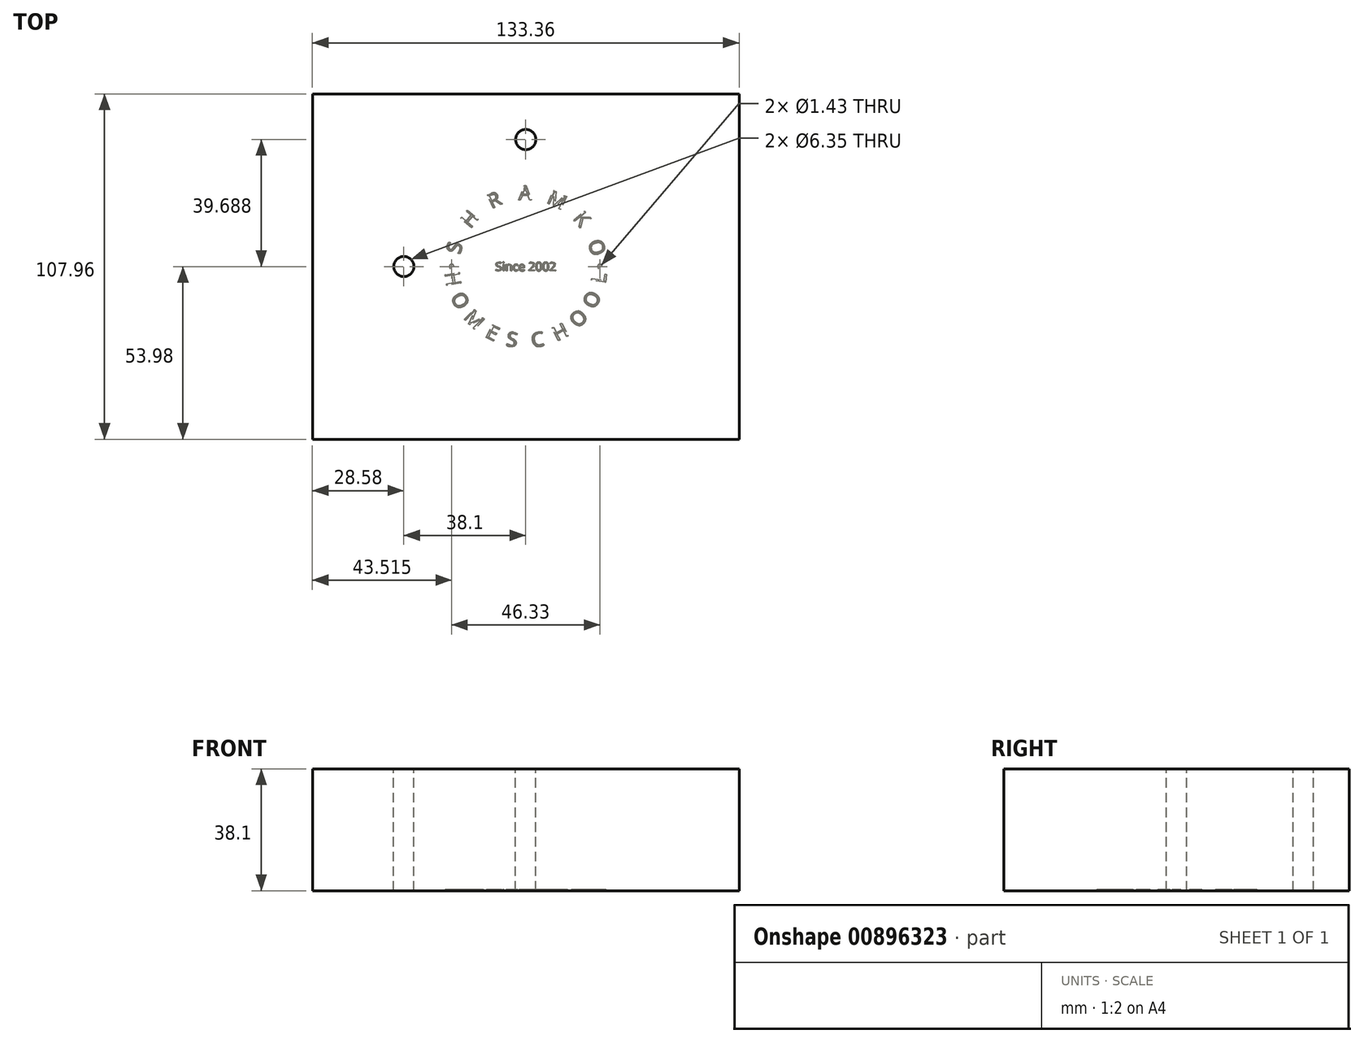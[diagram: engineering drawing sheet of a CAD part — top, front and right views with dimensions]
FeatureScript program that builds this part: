
annotation { "Feature Type Name" : "Feature", "Feature Type Description" : "" }
export const myFeature = defineFeature(function(context is Context, id is Id, definition is map)
    precondition{}
    {
        {
            var Q0;
            Q0=qCreatedBy(makeId("Top.planeOp"),FACE);
            var sketch = newSketch(context, id + "F0", { "sketchPlane" : qUnion([Q0])});
            skLineSegment(sketch, "E0.bottom", {"start": v(66.67, 53.98) * mm, "end": v(-66.68, 53.98) * mm});
            skLineSegment(sketch, "E0.top", {"start": v(66.68, -53.98) * mm, "end": v(-66.67, -53.98) * mm});
            skLineSegment(sketch, "E0.left", {"start": v(66.67, 53.98) * mm, "end": v(66.68, -53.98) * mm});
            skLineSegment(sketch, "E0.right", {"start": v(-66.68, 53.98) * mm, "end": v(-66.67, -53.98) * mm});
            skPoint(sketch, "E0.middle", {"position": v(0, 0) * mm});
            skSolve(sketch);
        }
        {
            var Q0;
            Q0 = qSketchRegion(id + "F0", true);
            extrude(context, id + "F1", {"entities" : qUnion([Q0]), "depth" : 38.1 * mm, "offsetDistance" : 25.4 * mm});
        }
        {
            var Q0;
            Q0=qCreatedBy(makeId("Top.planeOp"),FACE);
            var sketch = newSketch(context, id + "F2", { "sketchPlane" : qUnion([Q0])});
            skCircle(sketch, "E1", {"center": v(0, 0) * mm, "radius": 20.93 * mm, "construction": true});
            skCircle(sketch, "E2", {"center": v(0, 0) * mm, "radius": 25.4 * mm, "construction": true});
            skText(sketch, "E3", { "text": "S", "fontName": "OpenSans-Regular.ttf"});
            skText(sketch, "E4", { "text": "H", "fontName": "OpenSans-Regular.ttf"});
            skText(sketch, "E5", { "text": "R", "fontName": "OpenSans-Regular.ttf"});
            skText(sketch, "E6", { "text": "A", "fontName": "OpenSans-Regular.ttf"});
            skText(sketch, "E7", { "text": "M", "fontName": "OpenSans-Regular.ttf"});
            skText(sketch, "E8", { "text": "K", "fontName": "OpenSans-Regular.ttf"});
            skText(sketch, "E9", { "text": "O", "fontName": "OpenSans-Regular.ttf"});
            skCircle(sketch, "E10", {"center": v(-23.16, 0) * mm, "radius": 0.71 * mm});
            skCircle(sketch, "E11", {"center": v(23.16, 0) * mm, "radius": 0.71 * mm});
            skLineSegment(sketch, "E12", {"start": v(0, 0) * mm, "end": v(0, 25.3) * mm, "construction": true});
            skText(sketch, "E13", { "text": "H", "fontName": "OpenSans-Regular.ttf"});
            skText(sketch, "E14", { "text": "O", "fontName": "OpenSans-Regular.ttf"});
            skText(sketch, "E15", { "text": "M", "fontName": "OpenSans-Regular.ttf"});
            skText(sketch, "E16", { "text": "S", "fontName": "OpenSans-Regular.ttf"});
            skText(sketch, "E17", { "text": "C", "fontName": "OpenSans-Regular.ttf"});
            skText(sketch, "E18", { "text": "O", "fontName": "OpenSans-Regular.ttf"});
            skText(sketch, "E19", { "text": "O", "fontName": "OpenSans-Regular.ttf"});
            skText(sketch, "E20", { "text": "L", "fontName": "OpenSans-Regular.ttf"});
            skText(sketch, "E21", { "text": "E", "fontName": "OpenSans-Regular.ttf"});
            skText(sketch, "E22", { "text": "H", "fontName": "OpenSans-Regular.ttf"});
            const initialGuessF2  = {"E3": [-0.0206, 0.0037, 0.25882, 0.96593, 0.00448], "E4": [-0.01736, 0.0117, 0.64279, 0.76604, 0.0045], "E5": [-0.01068, 0.018, 0.9063, 0.42262, 0.00449], "E6": [-0.0022, 0.02078, 1, 0, 0.00452], "E7": [0.0063, 0.01996, 0.9063, -0.42262, 0.0045], "E8": [0.0146, 0.015, 0.64279, -0.76604, 0.00449], "E9": [0.02505, 0.00418, -0.25882, 0.96593, 0.0045], "E13": [-0.02532, -0.00198, 0.16413, -0.98644, 0.0045], "E14": [-0.02356, -0.00948, 0.46092, -0.88744, 0.0045], "E15": [-0.01966, -0.01609, 0.7126, -0.70157, 0.0045], "E16": [-0.0063, -0.02473, 0.98888, -0.14873, 0.00447], "E17": [0.0021, -0.02531, 0.98644, 0.16413, 0.00449], "E18": [0.0163, -0.01948, 0.70157, 0.7126, 0.0045], "E19": [0.02152, -0.01349, 0.44703, 0.89452, 0.0045], "E20": [0.0248, -0.0055, 0.14873, 0.98888, 0.00448], "E21": [-0.01289, -0.02189, 0.89452, -0.44703, 0.00448], "E22": [0.00971, -0.02347, 0.88744, 0.46092, 0.0045]};
            skSetInitialGuess(sketch, initialGuessF2);
            skSolve(sketch);
        }
        {
            var Q0;
            Q0 = qSketchRegion(id + "F2", true);
            extrude(context, id + "F3", {"entities" : qUnion([Q0]), "operationType" : NewBodyOperationType.REMOVE, "depth" : 0.36 * mm, "offsetDistance" : 25.4 * mm});
        }
        {
            var Q0;
            Q0=makeQuery(id+"F3.boolean.opBoolean","COPY",FACE,{"derivedFrom":makeQuery(id+"F3.opExtrude","CAP_FACE",FACE,{"disambiguationData":[OSD([sQuery(id+"F2.wireOp",EDGE,"E13.sketch_text.stroke-0"),sQuery(id+"F2.wireOp",EDGE,"E13.sketch_text.stroke-1"),sQuery(id+"F2.wireOp",EDGE,"E13.sketch_text.stroke-2"),sQuery(id+"F2.wireOp",EDGE,"E13.sketch_text.stroke-3"),sQuery(id+"F2.wireOp",EDGE,"E13.sketch_text.stroke-4"),sQuery(id+"F2.wireOp",EDGE,"E13.sketch_text.stroke-5"),sQuery(id+"F2.wireOp",EDGE,"E13.sketch_text.stroke-6"),sQuery(id+"F2.wireOp",EDGE,"E13.sketch_text.stroke-7"),sQuery(id+"F2.wireOp",EDGE,"E13.sketch_text.stroke-8"),sQuery(id+"F2.wireOp",EDGE,"E13.sketch_text.stroke-9"),sQuery(id+"F2.wireOp",EDGE,"E13.sketch_text.stroke-10"),sQuery(id+"F2.wireOp",EDGE,"E13.sketch_text.stroke-11")])],"isStart":false})});
            var Q1;
            Q1=makeQuery(id+"F3.boolean.opBoolean","COPY",FACE,{"derivedFrom":makeQuery(id+"F3.opExtrude","CAP_FACE",FACE,{"disambiguationData":[OSD([sQuery(id+"F2.wireOp",EDGE,"E14.sketch_text.stroke-0"),sQuery(id+"F2.wireOp",EDGE,"E14.sketch_text.stroke-1"),sQuery(id+"F2.wireOp",EDGE,"E14.sketch_text.stroke-2"),sQuery(id+"F2.wireOp",EDGE,"E14.sketch_text.stroke-3"),sQuery(id+"F2.wireOp",EDGE,"E14.sketch_text.stroke-4"),sQuery(id+"F2.wireOp",EDGE,"E14.sketch_text.stroke-5"),sQuery(id+"F2.wireOp",EDGE,"E14.sketch_text.stroke-6"),sQuery(id+"F2.wireOp",EDGE,"E14.sketch_text.stroke-7"),sQuery(id+"F2.wireOp",EDGE,"E14.sketch_text.stroke-8"),sQuery(id+"F2.wireOp",EDGE,"E14.sketch_text.stroke-9"),sQuery(id+"F2.wireOp",EDGE,"E14.sketch_text.stroke-10"),sQuery(id+"F2.wireOp",EDGE,"E14.sketch_text.stroke-11"),sQuery(id+"F2.wireOp",EDGE,"E14.sketch_text.stroke-12"),sQuery(id+"F2.wireOp",EDGE,"E14.sketch_text.stroke-13"),sQuery(id+"F2.wireOp",EDGE,"E14.sketch_text.stroke-14"),sQuery(id+"F2.wireOp",EDGE,"E14.sketch_text.stroke-15")])],"isStart":false})});
            var Q2;
            Q2=makeQuery(id+"F3.boolean.opBoolean","COPY",FACE,{"derivedFrom":makeQuery(id+"F3.opExtrude","CAP_FACE",FACE,{"disambiguationData":[OSD([sQuery(id+"F2.wireOp",EDGE,"E15.sketch_text.stroke-0"),sQuery(id+"F2.wireOp",EDGE,"E15.sketch_text.stroke-1"),sQuery(id+"F2.wireOp",EDGE,"E15.sketch_text.stroke-2"),sQuery(id+"F2.wireOp",EDGE,"E15.sketch_text.stroke-3"),sQuery(id+"F2.wireOp",EDGE,"E15.sketch_text.stroke-4"),sQuery(id+"F2.wireOp",EDGE,"E15.sketch_text.stroke-5"),sQuery(id+"F2.wireOp",EDGE,"E15.sketch_text.stroke-6"),sQuery(id+"F2.wireOp",EDGE,"E15.sketch_text.stroke-7"),sQuery(id+"F2.wireOp",EDGE,"E15.sketch_text.stroke-8"),sQuery(id+"F2.wireOp",EDGE,"E15.sketch_text.stroke-9"),sQuery(id+"F2.wireOp",EDGE,"E15.sketch_text.stroke-10"),sQuery(id+"F2.wireOp",EDGE,"E15.sketch_text.stroke-11"),sQuery(id+"F2.wireOp",EDGE,"E15.sketch_text.stroke-12"),sQuery(id+"F2.wireOp",EDGE,"E15.sketch_text.stroke-13"),sQuery(id+"F2.wireOp",EDGE,"E15.sketch_text.stroke-14"),sQuery(id+"F2.wireOp",EDGE,"E15.sketch_text.stroke-15"),sQuery(id+"F2.wireOp",EDGE,"E15.sketch_text.stroke-16"),sQuery(id+"F2.wireOp",EDGE,"E15.sketch_text.stroke-17")])],"isStart":false})});
            var Q3;
            Q3=makeQuery(id+"F3.boolean.opBoolean","COPY",EDGE,{"derivedFrom":makeQuery(id+"F3.opExtrude","CAP_EDGE",EDGE,{"disambiguationData":[OSD([sQuery(id+"F2.wireOp",EDGE,"E10")])],"isStart":false})});
            var Q4;
            Q4=makeQuery(id+"F3.boolean.opBoolean","COPY",FACE,{"derivedFrom":makeQuery(id+"F3.opExtrude","CAP_FACE",FACE,{"disambiguationData":[OSD([sQuery(id+"F2.wireOp",EDGE,"E3.sketch_text.stroke-0"),sQuery(id+"F2.wireOp",EDGE,"E3.sketch_text.stroke-1"),sQuery(id+"F2.wireOp",EDGE,"E3.sketch_text.stroke-2"),sQuery(id+"F2.wireOp",EDGE,"E3.sketch_text.stroke-3"),sQuery(id+"F2.wireOp",EDGE,"E3.sketch_text.stroke-4"),sQuery(id+"F2.wireOp",EDGE,"E3.sketch_text.stroke-5"),sQuery(id+"F2.wireOp",EDGE,"E3.sketch_text.stroke-6"),sQuery(id+"F2.wireOp",EDGE,"E3.sketch_text.stroke-7"),sQuery(id+"F2.wireOp",EDGE,"E3.sketch_text.stroke-8"),sQuery(id+"F2.wireOp",EDGE,"E3.sketch_text.stroke-9"),sQuery(id+"F2.wireOp",EDGE,"E3.sketch_text.stroke-10"),sQuery(id+"F2.wireOp",EDGE,"E3.sketch_text.stroke-11"),sQuery(id+"F2.wireOp",EDGE,"E3.sketch_text.stroke-12"),sQuery(id+"F2.wireOp",EDGE,"E3.sketch_text.stroke-13"),sQuery(id+"F2.wireOp",EDGE,"E3.sketch_text.stroke-14"),sQuery(id+"F2.wireOp",EDGE,"E3.sketch_text.stroke-15"),sQuery(id+"F2.wireOp",EDGE,"E3.sketch_text.stroke-16"),sQuery(id+"F2.wireOp",EDGE,"E3.sketch_text.stroke-17"),sQuery(id+"F2.wireOp",EDGE,"E3.sketch_text.stroke-18"),sQuery(id+"F2.wireOp",EDGE,"E3.sketch_text.stroke-19"),sQuery(id+"F2.wireOp",EDGE,"E3.sketch_text.stroke-20"),sQuery(id+"F2.wireOp",EDGE,"E3.sketch_text.stroke-21"),sQuery(id+"F2.wireOp",EDGE,"E3.sketch_text.stroke-22"),sQuery(id+"F2.wireOp",EDGE,"E3.sketch_text.stroke-23"),sQuery(id+"F2.wireOp",EDGE,"E3.sketch_text.stroke-24")])],"isStart":false})});
            var Q5;
            Q5=makeQuery(id+"F3.boolean.opBoolean","COPY",FACE,{"derivedFrom":makeQuery(id+"F3.opExtrude","CAP_FACE",FACE,{"disambiguationData":[OSD([sQuery(id+"F2.wireOp",EDGE,"E4.sketch_text.stroke-0"),sQuery(id+"F2.wireOp",EDGE,"E4.sketch_text.stroke-1"),sQuery(id+"F2.wireOp",EDGE,"E4.sketch_text.stroke-2"),sQuery(id+"F2.wireOp",EDGE,"E4.sketch_text.stroke-3"),sQuery(id+"F2.wireOp",EDGE,"E4.sketch_text.stroke-4"),sQuery(id+"F2.wireOp",EDGE,"E4.sketch_text.stroke-5"),sQuery(id+"F2.wireOp",EDGE,"E4.sketch_text.stroke-6"),sQuery(id+"F2.wireOp",EDGE,"E4.sketch_text.stroke-7"),sQuery(id+"F2.wireOp",EDGE,"E4.sketch_text.stroke-8"),sQuery(id+"F2.wireOp",EDGE,"E4.sketch_text.stroke-9"),sQuery(id+"F2.wireOp",EDGE,"E4.sketch_text.stroke-10"),sQuery(id+"F2.wireOp",EDGE,"E4.sketch_text.stroke-11")])],"isStart":false})});
            var Q6;
            Q6=makeQuery(id+"F3.boolean.opBoolean","COPY",FACE,{"derivedFrom":makeQuery(id+"F3.opExtrude","CAP_FACE",FACE,{"disambiguationData":[OSD([sQuery(id+"F2.wireOp",EDGE,"E5.sketch_text.stroke-0"),sQuery(id+"F2.wireOp",EDGE,"E5.sketch_text.stroke-1"),sQuery(id+"F2.wireOp",EDGE,"E5.sketch_text.stroke-2"),sQuery(id+"F2.wireOp",EDGE,"E5.sketch_text.stroke-3"),sQuery(id+"F2.wireOp",EDGE,"E5.sketch_text.stroke-4"),sQuery(id+"F2.wireOp",EDGE,"E5.sketch_text.stroke-5"),sQuery(id+"F2.wireOp",EDGE,"E5.sketch_text.stroke-6"),sQuery(id+"F2.wireOp",EDGE,"E5.sketch_text.stroke-7"),sQuery(id+"F2.wireOp",EDGE,"E5.sketch_text.stroke-8"),sQuery(id+"F2.wireOp",EDGE,"E5.sketch_text.stroke-9"),sQuery(id+"F2.wireOp",EDGE,"E5.sketch_text.stroke-10"),sQuery(id+"F2.wireOp",EDGE,"E5.sketch_text.stroke-11"),sQuery(id+"F2.wireOp",EDGE,"E5.sketch_text.stroke-12"),sQuery(id+"F2.wireOp",EDGE,"E5.sketch_text.stroke-13"),sQuery(id+"F2.wireOp",EDGE,"E5.sketch_text.stroke-14"),sQuery(id+"F2.wireOp",EDGE,"E5.sketch_text.stroke-15"),sQuery(id+"F2.wireOp",EDGE,"E5.sketch_text.stroke-16"),sQuery(id+"F2.wireOp",EDGE,"E5.sketch_text.stroke-17")])],"isStart":false})});
            var Q7;
            Q7=makeQuery(id+"F3.boolean.opBoolean","COPY",FACE,{"derivedFrom":makeQuery(id+"F3.opExtrude","CAP_FACE",FACE,{"disambiguationData":[OSD([sQuery(id+"F2.wireOp",EDGE,"E6.sketch_text.stroke-0"),sQuery(id+"F2.wireOp",EDGE,"E6.sketch_text.stroke-1"),sQuery(id+"F2.wireOp",EDGE,"E6.sketch_text.stroke-2"),sQuery(id+"F2.wireOp",EDGE,"E6.sketch_text.stroke-3"),sQuery(id+"F2.wireOp",EDGE,"E6.sketch_text.stroke-4"),sQuery(id+"F2.wireOp",EDGE,"E6.sketch_text.stroke-5"),sQuery(id+"F2.wireOp",EDGE,"E6.sketch_text.stroke-6"),sQuery(id+"F2.wireOp",EDGE,"E6.sketch_text.stroke-7"),sQuery(id+"F2.wireOp",EDGE,"E6.sketch_text.stroke-8"),sQuery(id+"F2.wireOp",EDGE,"E6.sketch_text.stroke-9"),sQuery(id+"F2.wireOp",EDGE,"E6.sketch_text.stroke-10"),sQuery(id+"F2.wireOp",EDGE,"E6.sketch_text.stroke-11"),sQuery(id+"F2.wireOp",EDGE,"E6.sketch_text.stroke-12")])],"isStart":false})});
            var Q8;
            Q8=makeQuery(id+"F3.boolean.opBoolean","COPY",FACE,{"derivedFrom":makeQuery(id+"F3.opExtrude","CAP_FACE",FACE,{"disambiguationData":[OSD([sQuery(id+"F2.wireOp",EDGE,"E7.sketch_text.stroke-0"),sQuery(id+"F2.wireOp",EDGE,"E7.sketch_text.stroke-1"),sQuery(id+"F2.wireOp",EDGE,"E7.sketch_text.stroke-2"),sQuery(id+"F2.wireOp",EDGE,"E7.sketch_text.stroke-3"),sQuery(id+"F2.wireOp",EDGE,"E7.sketch_text.stroke-4"),sQuery(id+"F2.wireOp",EDGE,"E7.sketch_text.stroke-5"),sQuery(id+"F2.wireOp",EDGE,"E7.sketch_text.stroke-6"),sQuery(id+"F2.wireOp",EDGE,"E7.sketch_text.stroke-7"),sQuery(id+"F2.wireOp",EDGE,"E7.sketch_text.stroke-8"),sQuery(id+"F2.wireOp",EDGE,"E7.sketch_text.stroke-9"),sQuery(id+"F2.wireOp",EDGE,"E7.sketch_text.stroke-10"),sQuery(id+"F2.wireOp",EDGE,"E7.sketch_text.stroke-11"),sQuery(id+"F2.wireOp",EDGE,"E7.sketch_text.stroke-12"),sQuery(id+"F2.wireOp",EDGE,"E7.sketch_text.stroke-13"),sQuery(id+"F2.wireOp",EDGE,"E7.sketch_text.stroke-14"),sQuery(id+"F2.wireOp",EDGE,"E7.sketch_text.stroke-15"),sQuery(id+"F2.wireOp",EDGE,"E7.sketch_text.stroke-16"),sQuery(id+"F2.wireOp",EDGE,"E7.sketch_text.stroke-17")])],"isStart":false})});
            var Q9;
            Q9=makeQuery(id+"F3.boolean.opBoolean","COPY",FACE,{"derivedFrom":makeQuery(id+"F3.opExtrude","CAP_FACE",FACE,{"disambiguationData":[OSD([sQuery(id+"F2.wireOp",EDGE,"E8.sketch_text.stroke-0"),sQuery(id+"F2.wireOp",EDGE,"E8.sketch_text.stroke-1"),sQuery(id+"F2.wireOp",EDGE,"E8.sketch_text.stroke-2"),sQuery(id+"F2.wireOp",EDGE,"E8.sketch_text.stroke-3"),sQuery(id+"F2.wireOp",EDGE,"E8.sketch_text.stroke-4"),sQuery(id+"F2.wireOp",EDGE,"E8.sketch_text.stroke-5"),sQuery(id+"F2.wireOp",EDGE,"E8.sketch_text.stroke-6"),sQuery(id+"F2.wireOp",EDGE,"E8.sketch_text.stroke-7"),sQuery(id+"F2.wireOp",EDGE,"E8.sketch_text.stroke-8"),sQuery(id+"F2.wireOp",EDGE,"E8.sketch_text.stroke-9"),sQuery(id+"F2.wireOp",EDGE,"E8.sketch_text.stroke-10"),sQuery(id+"F2.wireOp",EDGE,"E8.sketch_text.stroke-11")])],"isStart":false})});
            var Q10;
            Q10=makeQuery(id+"F3.boolean.opBoolean","COPY",FACE,{"derivedFrom":makeQuery(id+"F3.opExtrude","CAP_FACE",FACE,{"disambiguationData":[OSD([sQuery(id+"F2.wireOp",EDGE,"E21.sketch_text.stroke-0"),sQuery(id+"F2.wireOp",EDGE,"E21.sketch_text.stroke-1"),sQuery(id+"F2.wireOp",EDGE,"E21.sketch_text.stroke-2"),sQuery(id+"F2.wireOp",EDGE,"E21.sketch_text.stroke-3"),sQuery(id+"F2.wireOp",EDGE,"E21.sketch_text.stroke-4"),sQuery(id+"F2.wireOp",EDGE,"E21.sketch_text.stroke-5"),sQuery(id+"F2.wireOp",EDGE,"E21.sketch_text.stroke-6"),sQuery(id+"F2.wireOp",EDGE,"E21.sketch_text.stroke-7"),sQuery(id+"F2.wireOp",EDGE,"E21.sketch_text.stroke-8"),sQuery(id+"F2.wireOp",EDGE,"E21.sketch_text.stroke-9"),sQuery(id+"F2.wireOp",EDGE,"E21.sketch_text.stroke-10"),sQuery(id+"F2.wireOp",EDGE,"E21.sketch_text.stroke-11")])],"isStart":false})});
            var Q11;
            Q11=makeQuery(id+"F3.boolean.opBoolean","COPY",FACE,{"derivedFrom":makeQuery(id+"F3.opExtrude","CAP_FACE",FACE,{"disambiguationData":[OSD([sQuery(id+"F2.wireOp",EDGE,"E18.sketch_text.stroke-0"),sQuery(id+"F2.wireOp",EDGE,"E18.sketch_text.stroke-1"),sQuery(id+"F2.wireOp",EDGE,"E18.sketch_text.stroke-2"),sQuery(id+"F2.wireOp",EDGE,"E18.sketch_text.stroke-3"),sQuery(id+"F2.wireOp",EDGE,"E18.sketch_text.stroke-4"),sQuery(id+"F2.wireOp",EDGE,"E18.sketch_text.stroke-5"),sQuery(id+"F2.wireOp",EDGE,"E18.sketch_text.stroke-6"),sQuery(id+"F2.wireOp",EDGE,"E18.sketch_text.stroke-7"),sQuery(id+"F2.wireOp",EDGE,"E18.sketch_text.stroke-8"),sQuery(id+"F2.wireOp",EDGE,"E18.sketch_text.stroke-9"),sQuery(id+"F2.wireOp",EDGE,"E18.sketch_text.stroke-10"),sQuery(id+"F2.wireOp",EDGE,"E18.sketch_text.stroke-11"),sQuery(id+"F2.wireOp",EDGE,"E18.sketch_text.stroke-12"),sQuery(id+"F2.wireOp",EDGE,"E18.sketch_text.stroke-13"),sQuery(id+"F2.wireOp",EDGE,"E18.sketch_text.stroke-14"),sQuery(id+"F2.wireOp",EDGE,"E18.sketch_text.stroke-15")])],"isStart":false})});
            var Q12;
            Q12=makeQuery(id+"F3.boolean.opBoolean","COPY",FACE,{"derivedFrom":makeQuery(id+"F3.opExtrude","CAP_FACE",FACE,{"disambiguationData":[OSD([sQuery(id+"F2.wireOp",EDGE,"E17.sketch_text.stroke-0"),sQuery(id+"F2.wireOp",EDGE,"E17.sketch_text.stroke-1"),sQuery(id+"F2.wireOp",EDGE,"E17.sketch_text.stroke-2"),sQuery(id+"F2.wireOp",EDGE,"E17.sketch_text.stroke-3"),sQuery(id+"F2.wireOp",EDGE,"E17.sketch_text.stroke-4"),sQuery(id+"F2.wireOp",EDGE,"E17.sketch_text.stroke-5"),sQuery(id+"F2.wireOp",EDGE,"E17.sketch_text.stroke-6"),sQuery(id+"F2.wireOp",EDGE,"E17.sketch_text.stroke-7"),sQuery(id+"F2.wireOp",EDGE,"E17.sketch_text.stroke-8"),sQuery(id+"F2.wireOp",EDGE,"E17.sketch_text.stroke-9"),sQuery(id+"F2.wireOp",EDGE,"E17.sketch_text.stroke-10"),sQuery(id+"F2.wireOp",EDGE,"E17.sketch_text.stroke-11"),sQuery(id+"F2.wireOp",EDGE,"E17.sketch_text.stroke-12"),sQuery(id+"F2.wireOp",EDGE,"E17.sketch_text.stroke-13"),sQuery(id+"F2.wireOp",EDGE,"E17.sketch_text.stroke-14")])],"isStart":false})});
            var Q13;
            Q13=makeQuery(id+"F3.boolean.opBoolean","COPY",FACE,{"derivedFrom":makeQuery(id+"F3.opExtrude","CAP_FACE",FACE,{"disambiguationData":[OSD([sQuery(id+"F2.wireOp",EDGE,"E16.sketch_text.stroke-0"),sQuery(id+"F2.wireOp",EDGE,"E16.sketch_text.stroke-1"),sQuery(id+"F2.wireOp",EDGE,"E16.sketch_text.stroke-2"),sQuery(id+"F2.wireOp",EDGE,"E16.sketch_text.stroke-3"),sQuery(id+"F2.wireOp",EDGE,"E16.sketch_text.stroke-4"),sQuery(id+"F2.wireOp",EDGE,"E16.sketch_text.stroke-5"),sQuery(id+"F2.wireOp",EDGE,"E16.sketch_text.stroke-6"),sQuery(id+"F2.wireOp",EDGE,"E16.sketch_text.stroke-7"),sQuery(id+"F2.wireOp",EDGE,"E16.sketch_text.stroke-8"),sQuery(id+"F2.wireOp",EDGE,"E16.sketch_text.stroke-9"),sQuery(id+"F2.wireOp",EDGE,"E16.sketch_text.stroke-10"),sQuery(id+"F2.wireOp",EDGE,"E16.sketch_text.stroke-11"),sQuery(id+"F2.wireOp",EDGE,"E16.sketch_text.stroke-12"),sQuery(id+"F2.wireOp",EDGE,"E16.sketch_text.stroke-13"),sQuery(id+"F2.wireOp",EDGE,"E16.sketch_text.stroke-14"),sQuery(id+"F2.wireOp",EDGE,"E16.sketch_text.stroke-15"),sQuery(id+"F2.wireOp",EDGE,"E16.sketch_text.stroke-16"),sQuery(id+"F2.wireOp",EDGE,"E16.sketch_text.stroke-17"),sQuery(id+"F2.wireOp",EDGE,"E16.sketch_text.stroke-18"),sQuery(id+"F2.wireOp",EDGE,"E16.sketch_text.stroke-19"),sQuery(id+"F2.wireOp",EDGE,"E16.sketch_text.stroke-20"),sQuery(id+"F2.wireOp",EDGE,"E16.sketch_text.stroke-21"),sQuery(id+"F2.wireOp",EDGE,"E16.sketch_text.stroke-22"),sQuery(id+"F2.wireOp",EDGE,"E16.sketch_text.stroke-23"),sQuery(id+"F2.wireOp",EDGE,"E16.sketch_text.stroke-24")])],"isStart":false})});
            var Q14;
            Q14=makeQuery(id+"F3.boolean.opBoolean","COPY",FACE,{"derivedFrom":makeQuery(id+"F3.opExtrude","CAP_FACE",FACE,{"disambiguationData":[OSD([sQuery(id+"F2.wireOp",EDGE,"E19.sketch_text.stroke-0"),sQuery(id+"F2.wireOp",EDGE,"E19.sketch_text.stroke-1"),sQuery(id+"F2.wireOp",EDGE,"E19.sketch_text.stroke-2"),sQuery(id+"F2.wireOp",EDGE,"E19.sketch_text.stroke-3"),sQuery(id+"F2.wireOp",EDGE,"E19.sketch_text.stroke-4"),sQuery(id+"F2.wireOp",EDGE,"E19.sketch_text.stroke-5"),sQuery(id+"F2.wireOp",EDGE,"E19.sketch_text.stroke-6"),sQuery(id+"F2.wireOp",EDGE,"E19.sketch_text.stroke-7"),sQuery(id+"F2.wireOp",EDGE,"E19.sketch_text.stroke-8"),sQuery(id+"F2.wireOp",EDGE,"E19.sketch_text.stroke-9"),sQuery(id+"F2.wireOp",EDGE,"E19.sketch_text.stroke-10"),sQuery(id+"F2.wireOp",EDGE,"E19.sketch_text.stroke-11"),sQuery(id+"F2.wireOp",EDGE,"E19.sketch_text.stroke-12"),sQuery(id+"F2.wireOp",EDGE,"E19.sketch_text.stroke-13"),sQuery(id+"F2.wireOp",EDGE,"E19.sketch_text.stroke-14"),sQuery(id+"F2.wireOp",EDGE,"E19.sketch_text.stroke-15")])],"isStart":false})});
            var Q15;
            Q15=makeQuery(id+"F3.boolean.opBoolean","COPY",FACE,{"derivedFrom":makeQuery(id+"F3.opExtrude","CAP_FACE",FACE,{"disambiguationData":[OSD([sQuery(id+"F2.wireOp",EDGE,"E20.sketch_text.stroke-0"),sQuery(id+"F2.wireOp",EDGE,"E20.sketch_text.stroke-1"),sQuery(id+"F2.wireOp",EDGE,"E20.sketch_text.stroke-2"),sQuery(id+"F2.wireOp",EDGE,"E20.sketch_text.stroke-3"),sQuery(id+"F2.wireOp",EDGE,"E20.sketch_text.stroke-4"),sQuery(id+"F2.wireOp",EDGE,"E20.sketch_text.stroke-5")])],"isStart":false})});
            var Q16;
            Q16=makeQuery(id+"F3.boolean.opBoolean","COPY",FACE,{"derivedFrom":makeQuery(id+"F3.opExtrude","CAP_FACE",FACE,{"disambiguationData":[OSD([sQuery(id+"F2.wireOp",EDGE,"E9.sketch_text.stroke-0"),sQuery(id+"F2.wireOp",EDGE,"E9.sketch_text.stroke-1"),sQuery(id+"F2.wireOp",EDGE,"E9.sketch_text.stroke-2"),sQuery(id+"F2.wireOp",EDGE,"E9.sketch_text.stroke-3"),sQuery(id+"F2.wireOp",EDGE,"E9.sketch_text.stroke-4"),sQuery(id+"F2.wireOp",EDGE,"E9.sketch_text.stroke-5"),sQuery(id+"F2.wireOp",EDGE,"E9.sketch_text.stroke-6"),sQuery(id+"F2.wireOp",EDGE,"E9.sketch_text.stroke-7"),sQuery(id+"F2.wireOp",EDGE,"E9.sketch_text.stroke-8"),sQuery(id+"F2.wireOp",EDGE,"E9.sketch_text.stroke-9"),sQuery(id+"F2.wireOp",EDGE,"E9.sketch_text.stroke-10"),sQuery(id+"F2.wireOp",EDGE,"E9.sketch_text.stroke-11"),sQuery(id+"F2.wireOp",EDGE,"E9.sketch_text.stroke-12"),sQuery(id+"F2.wireOp",EDGE,"E9.sketch_text.stroke-13"),sQuery(id+"F2.wireOp",EDGE,"E9.sketch_text.stroke-14"),sQuery(id+"F2.wireOp",EDGE,"E9.sketch_text.stroke-15")])],"isStart":false})});
            var Q17;
            Q17=makeQuery(id+"F3.boolean.opBoolean","COPY",FACE,{"derivedFrom":makeQuery(id+"F3.opExtrude","CAP_FACE",FACE,{"disambiguationData":[OSD([sQuery(id+"F2.wireOp",EDGE,"E22.sketch_text.stroke-0"),sQuery(id+"F2.wireOp",EDGE,"E22.sketch_text.stroke-1"),sQuery(id+"F2.wireOp",EDGE,"E22.sketch_text.stroke-2"),sQuery(id+"F2.wireOp",EDGE,"E22.sketch_text.stroke-3"),sQuery(id+"F2.wireOp",EDGE,"E22.sketch_text.stroke-4"),sQuery(id+"F2.wireOp",EDGE,"E22.sketch_text.stroke-5"),sQuery(id+"F2.wireOp",EDGE,"E22.sketch_text.stroke-6"),sQuery(id+"F2.wireOp",EDGE,"E22.sketch_text.stroke-7"),sQuery(id+"F2.wireOp",EDGE,"E22.sketch_text.stroke-8"),sQuery(id+"F2.wireOp",EDGE,"E22.sketch_text.stroke-9"),sQuery(id+"F2.wireOp",EDGE,"E22.sketch_text.stroke-10"),sQuery(id+"F2.wireOp",EDGE,"E22.sketch_text.stroke-11")])],"isStart":false})});
            var Q18;
            Q18=makeQuery(id+"F3.boolean.opBoolean","COPY",EDGE,{"derivedFrom":makeQuery(id+"F3.opExtrude","CAP_EDGE",EDGE,{"disambiguationData":[OSD([sQuery(id+"F2.wireOp",EDGE,"E11")])],"isStart":false})});
            fillet(context, id + "F4", {"entities" : qUnion([Q0, Q1, Q2, Q3, Q4, Q5, Q6, Q7, Q8, Q9, Q10, Q11, Q12, Q13, Q14, Q15, Q16, Q17, Q18]), "radius" : 0.2 * mm, "tangentPropagation" : true, "allowEdgeOverflow" : false});
        }
        {
            var Q0;
            Q0=makeQuery(id+"F1.opExtrude","CAP_FACE",FACE,{"disambiguationData":[OSD([sQuery(id+"F0.wireOp",EDGE,"E0.bottom"),sQuery(id+"F0.wireOp",EDGE,"E0.top"),sQuery(id+"F0.wireOp",EDGE,"E0.left"),sQuery(id+"F0.wireOp",EDGE,"E0.right")])],"isStart":false});
            var sketch = newSketch(context, id + "F5", { "sketchPlane" : qUnion([Q0])});
            skCircle(sketch, "E23", {"center": v(-38.1, 0) * mm, "radius": 3.18 * mm});
            skCircle(sketch, "E24", {"center": v(0, 39.69) * mm, "radius": 3.18 * mm});
            skLineSegment(sketch, "E25", {"start": v(-38.1, 0) * mm, "end": v(0, 0) * mm, "construction": true});
            skLineSegment(sketch, "E26", {"start": v(0, 0) * mm, "end": v(0, 39.69) * mm, "construction": true});
            skLineSegment(sketch, "E27.bottom", {"start": v(66.68, 53.97) * mm, "end": v(-66.68, 53.97) * mm, "construction": true});
            skLineSegment(sketch, "E27.top", {"start": v(66.68, -53.98) * mm, "end": v(-66.68, -53.98) * mm, "construction": true});
            skLineSegment(sketch, "E27.left", {"start": v(66.67, 53.97) * mm, "end": v(66.68, -53.97) * mm, "construction": true});
            skLineSegment(sketch, "E27.right", {"start": v(-66.68, 53.97) * mm, "end": v(-66.68, -53.97) * mm, "construction": true});
            skPoint(sketch, "E27.middle", {"position": v(0, 0) * mm});
            skSolve(sketch);
        }
        {
            var Q0;
            Q0 = qSketchRegion(id + "F5", true);
            extrude(context, id + "F6", {"entities" : qUnion([Q0]), "operationType" : NewBodyOperationType.REMOVE, "endBound" : BoundingType.THROUGH_ALL, "oppositeDirection" : true, "depth" : 25.4 * mm, "offsetDistance" : 25.4 * mm});
        }
        {
            var Q0;
            Q0=qCreatedBy(makeId("Top.planeOp"),FACE);
            var sketch = newSketch(context, id + "F7", { "sketchPlane" : qUnion([Q0])});
            skText(sketch, "E28", { "text": "Since 2002", "fontName": "OpenSans-Regular.ttf"});
            const initialGuessF7  = {"E28": [-0.00952, -0.00137, 1, 0, 0.00274]};
            skSetInitialGuess(sketch, initialGuessF7);
            skSolve(sketch);
        }
        {
            var Q0;
            Q0 = qSketchRegion(id + "F7", true);
            extrude(context, id + "F8", {"entities" : qUnion([Q0]), "operationType" : NewBodyOperationType.REMOVE, "depth" : 0.36 * mm, "offsetDistance" : 25.4 * mm});
        }
        {
            var Q0;
            Q0=makeQuery(id+"F8.boolean.opBoolean","COPY",FACE,{"derivedFrom":makeQuery(id+"F8.opExtrude","CAP_FACE",FACE,{"disambiguationData":[OSD([sQuery(id+"F7.wireOp",EDGE,"E28.sketch_text.stroke-0"),sQuery(id+"F7.wireOp",EDGE,"E28.sketch_text.stroke-1"),sQuery(id+"F7.wireOp",EDGE,"E28.sketch_text.stroke-2"),sQuery(id+"F7.wireOp",EDGE,"E28.sketch_text.stroke-3"),sQuery(id+"F7.wireOp",EDGE,"E28.sketch_text.stroke-4"),sQuery(id+"F7.wireOp",EDGE,"E28.sketch_text.stroke-5"),sQuery(id+"F7.wireOp",EDGE,"E28.sketch_text.stroke-6"),sQuery(id+"F7.wireOp",EDGE,"E28.sketch_text.stroke-7"),sQuery(id+"F7.wireOp",EDGE,"E28.sketch_text.stroke-8"),sQuery(id+"F7.wireOp",EDGE,"E28.sketch_text.stroke-9"),sQuery(id+"F7.wireOp",EDGE,"E28.sketch_text.stroke-10"),sQuery(id+"F7.wireOp",EDGE,"E28.sketch_text.stroke-11"),sQuery(id+"F7.wireOp",EDGE,"E28.sketch_text.stroke-12"),sQuery(id+"F7.wireOp",EDGE,"E28.sketch_text.stroke-13"),sQuery(id+"F7.wireOp",EDGE,"E28.sketch_text.stroke-14"),sQuery(id+"F7.wireOp",EDGE,"E28.sketch_text.stroke-15"),sQuery(id+"F7.wireOp",EDGE,"E28.sketch_text.stroke-16"),sQuery(id+"F7.wireOp",EDGE,"E28.sketch_text.stroke-17"),sQuery(id+"F7.wireOp",EDGE,"E28.sketch_text.stroke-18"),sQuery(id+"F7.wireOp",EDGE,"E28.sketch_text.stroke-19"),sQuery(id+"F7.wireOp",EDGE,"E28.sketch_text.stroke-20"),sQuery(id+"F7.wireOp",EDGE,"E28.sketch_text.stroke-21"),sQuery(id+"F7.wireOp",EDGE,"E28.sketch_text.stroke-22"),sQuery(id+"F7.wireOp",EDGE,"E28.sketch_text.stroke-23"),sQuery(id+"F7.wireOp",EDGE,"E28.sketch_text.stroke-24")])],"isStart":false})});
            var Q1;
            Q1=makeQuery(id+"F8.boolean.opBoolean","COPY",FACE,{"derivedFrom":makeQuery(id+"F8.opExtrude","CAP_FACE",FACE,{"disambiguationData":[OSD([sQuery(id+"F7.wireOp",EDGE,"E28.sketch_text.stroke-25"),sQuery(id+"F7.wireOp",EDGE,"E28.sketch_text.stroke-26"),sQuery(id+"F7.wireOp",EDGE,"E28.sketch_text.stroke-27"),sQuery(id+"F7.wireOp",EDGE,"E28.sketch_text.stroke-28")])],"isStart":false})});
            var Q2;
            Q2=makeQuery(id+"F8.boolean.opBoolean","COPY",FACE,{"derivedFrom":makeQuery(id+"F8.opExtrude","CAP_FACE",FACE,{"disambiguationData":[OSD([sQuery(id+"F7.wireOp",EDGE,"E28.sketch_text.stroke-37"),sQuery(id+"F7.wireOp",EDGE,"E28.sketch_text.stroke-38"),sQuery(id+"F7.wireOp",EDGE,"E28.sketch_text.stroke-39"),sQuery(id+"F7.wireOp",EDGE,"E28.sketch_text.stroke-40"),sQuery(id+"F7.wireOp",EDGE,"E28.sketch_text.stroke-41"),sQuery(id+"F7.wireOp",EDGE,"E28.sketch_text.stroke-42"),sQuery(id+"F7.wireOp",EDGE,"E28.sketch_text.stroke-43"),sQuery(id+"F7.wireOp",EDGE,"E28.sketch_text.stroke-44"),sQuery(id+"F7.wireOp",EDGE,"E28.sketch_text.stroke-45"),sQuery(id+"F7.wireOp",EDGE,"E28.sketch_text.stroke-46"),sQuery(id+"F7.wireOp",EDGE,"E28.sketch_text.stroke-47"),sQuery(id+"F7.wireOp",EDGE,"E28.sketch_text.stroke-48"),sQuery(id+"F7.wireOp",EDGE,"E28.sketch_text.stroke-49"),sQuery(id+"F7.wireOp",EDGE,"E28.sketch_text.stroke-50"),sQuery(id+"F7.wireOp",EDGE,"E28.sketch_text.stroke-51"),sQuery(id+"F7.wireOp",EDGE,"E28.sketch_text.stroke-52"),sQuery(id+"F7.wireOp",EDGE,"E28.sketch_text.stroke-53")])],"isStart":false})});
            var Q3;
            Q3=makeQuery(id+"F8.boolean.opBoolean","COPY",FACE,{"derivedFrom":makeQuery(id+"F8.opExtrude","CAP_FACE",FACE,{"disambiguationData":[OSD([sQuery(id+"F7.wireOp",EDGE,"E28.sketch_text.stroke-54"),sQuery(id+"F7.wireOp",EDGE,"E28.sketch_text.stroke-55"),sQuery(id+"F7.wireOp",EDGE,"E28.sketch_text.stroke-56"),sQuery(id+"F7.wireOp",EDGE,"E28.sketch_text.stroke-57"),sQuery(id+"F7.wireOp",EDGE,"E28.sketch_text.stroke-58"),sQuery(id+"F7.wireOp",EDGE,"E28.sketch_text.stroke-59"),sQuery(id+"F7.wireOp",EDGE,"E28.sketch_text.stroke-60"),sQuery(id+"F7.wireOp",EDGE,"E28.sketch_text.stroke-61"),sQuery(id+"F7.wireOp",EDGE,"E28.sketch_text.stroke-62"),sQuery(id+"F7.wireOp",EDGE,"E28.sketch_text.stroke-63"),sQuery(id+"F7.wireOp",EDGE,"E28.sketch_text.stroke-64"),sQuery(id+"F7.wireOp",EDGE,"E28.sketch_text.stroke-65"),sQuery(id+"F7.wireOp",EDGE,"E28.sketch_text.stroke-66"),sQuery(id+"F7.wireOp",EDGE,"E28.sketch_text.stroke-67"),sQuery(id+"F7.wireOp",EDGE,"E28.sketch_text.stroke-68")])],"isStart":false})});
            var Q4;
            Q4=makeQuery(id+"F8.boolean.opBoolean","COPY",FACE,{"derivedFrom":makeQuery(id+"F8.opExtrude","CAP_FACE",FACE,{"disambiguationData":[OSD([sQuery(id+"F7.wireOp",EDGE,"E28.sketch_text.stroke-69"),sQuery(id+"F7.wireOp",EDGE,"E28.sketch_text.stroke-70"),sQuery(id+"F7.wireOp",EDGE,"E28.sketch_text.stroke-71"),sQuery(id+"F7.wireOp",EDGE,"E28.sketch_text.stroke-72"),sQuery(id+"F7.wireOp",EDGE,"E28.sketch_text.stroke-73"),sQuery(id+"F7.wireOp",EDGE,"E28.sketch_text.stroke-74"),sQuery(id+"F7.wireOp",EDGE,"E28.sketch_text.stroke-75"),sQuery(id+"F7.wireOp",EDGE,"E28.sketch_text.stroke-76"),sQuery(id+"F7.wireOp",EDGE,"E28.sketch_text.stroke-77"),sQuery(id+"F7.wireOp",EDGE,"E28.sketch_text.stroke-78"),sQuery(id+"F7.wireOp",EDGE,"E28.sketch_text.stroke-79"),sQuery(id+"F7.wireOp",EDGE,"E28.sketch_text.stroke-80"),sQuery(id+"F7.wireOp",EDGE,"E28.sketch_text.stroke-81"),sQuery(id+"F7.wireOp",EDGE,"E28.sketch_text.stroke-82"),sQuery(id+"F7.wireOp",EDGE,"E28.sketch_text.stroke-83"),sQuery(id+"F7.wireOp",EDGE,"E28.sketch_text.stroke-84"),sQuery(id+"F7.wireOp",EDGE,"E28.sketch_text.stroke-85"),sQuery(id+"F7.wireOp",EDGE,"E28.sketch_text.stroke-86"),sQuery(id+"F7.wireOp",EDGE,"E28.sketch_text.stroke-87")])],"isStart":false})});
            var Q5;
            Q5=makeQuery(id+"F8.boolean.opBoolean","COPY",FACE,{"derivedFrom":makeQuery(id+"F8.opExtrude","CAP_FACE",FACE,{"disambiguationData":[OSD([sQuery(id+"F7.wireOp",EDGE,"E28.sketch_text.stroke-88"),sQuery(id+"F7.wireOp",EDGE,"E28.sketch_text.stroke-89"),sQuery(id+"F7.wireOp",EDGE,"E28.sketch_text.stroke-90"),sQuery(id+"F7.wireOp",EDGE,"E28.sketch_text.stroke-91"),sQuery(id+"F7.wireOp",EDGE,"E28.sketch_text.stroke-92"),sQuery(id+"F7.wireOp",EDGE,"E28.sketch_text.stroke-93"),sQuery(id+"F7.wireOp",EDGE,"E28.sketch_text.stroke-94"),sQuery(id+"F7.wireOp",EDGE,"E28.sketch_text.stroke-95"),sQuery(id+"F7.wireOp",EDGE,"E28.sketch_text.stroke-96"),sQuery(id+"F7.wireOp",EDGE,"E28.sketch_text.stroke-97"),sQuery(id+"F7.wireOp",EDGE,"E28.sketch_text.stroke-98"),sQuery(id+"F7.wireOp",EDGE,"E28.sketch_text.stroke-99"),sQuery(id+"F7.wireOp",EDGE,"E28.sketch_text.stroke-100"),sQuery(id+"F7.wireOp",EDGE,"E28.sketch_text.stroke-101"),sQuery(id+"F7.wireOp",EDGE,"E28.sketch_text.stroke-102"),sQuery(id+"F7.wireOp",EDGE,"E28.sketch_text.stroke-103"),sQuery(id+"F7.wireOp",EDGE,"E28.sketch_text.stroke-104"),sQuery(id+"F7.wireOp",EDGE,"E28.sketch_text.stroke-105"),sQuery(id+"F7.wireOp",EDGE,"E28.sketch_text.stroke-106"),sQuery(id+"F7.wireOp",EDGE,"E28.sketch_text.stroke-107")])],"isStart":false})});
            var Q6;
            Q6=makeQuery(id+"F8.boolean.opBoolean","COPY",FACE,{"derivedFrom":makeQuery(id+"F8.opExtrude","CAP_FACE",FACE,{"disambiguationData":[OSD([sQuery(id+"F7.wireOp",EDGE,"E28.sketch_text.stroke-108"),sQuery(id+"F7.wireOp",EDGE,"E28.sketch_text.stroke-109"),sQuery(id+"F7.wireOp",EDGE,"E28.sketch_text.stroke-110"),sQuery(id+"F7.wireOp",EDGE,"E28.sketch_text.stroke-111"),sQuery(id+"F7.wireOp",EDGE,"E28.sketch_text.stroke-112"),sQuery(id+"F7.wireOp",EDGE,"E28.sketch_text.stroke-113"),sQuery(id+"F7.wireOp",EDGE,"E28.sketch_text.stroke-114"),sQuery(id+"F7.wireOp",EDGE,"E28.sketch_text.stroke-115"),sQuery(id+"F7.wireOp",EDGE,"E28.sketch_text.stroke-116"),sQuery(id+"F7.wireOp",EDGE,"E28.sketch_text.stroke-117"),sQuery(id+"F7.wireOp",EDGE,"E28.sketch_text.stroke-118"),sQuery(id+"F7.wireOp",EDGE,"E28.sketch_text.stroke-119"),sQuery(id+"F7.wireOp",EDGE,"E28.sketch_text.stroke-120"),sQuery(id+"F7.wireOp",EDGE,"E28.sketch_text.stroke-121"),sQuery(id+"F7.wireOp",EDGE,"E28.sketch_text.stroke-122"),sQuery(id+"F7.wireOp",EDGE,"E28.sketch_text.stroke-123")])],"isStart":false})});
            var Q7;
            Q7=makeQuery(id+"F8.boolean.opBoolean","COPY",FACE,{"derivedFrom":makeQuery(id+"F8.opExtrude","CAP_FACE",FACE,{"disambiguationData":[OSD([sQuery(id+"F7.wireOp",EDGE,"E28.sketch_text.stroke-124"),sQuery(id+"F7.wireOp",EDGE,"E28.sketch_text.stroke-125"),sQuery(id+"F7.wireOp",EDGE,"E28.sketch_text.stroke-126"),sQuery(id+"F7.wireOp",EDGE,"E28.sketch_text.stroke-127"),sQuery(id+"F7.wireOp",EDGE,"E28.sketch_text.stroke-128"),sQuery(id+"F7.wireOp",EDGE,"E28.sketch_text.stroke-129"),sQuery(id+"F7.wireOp",EDGE,"E28.sketch_text.stroke-130"),sQuery(id+"F7.wireOp",EDGE,"E28.sketch_text.stroke-131"),sQuery(id+"F7.wireOp",EDGE,"E28.sketch_text.stroke-132"),sQuery(id+"F7.wireOp",EDGE,"E28.sketch_text.stroke-133"),sQuery(id+"F7.wireOp",EDGE,"E28.sketch_text.stroke-134"),sQuery(id+"F7.wireOp",EDGE,"E28.sketch_text.stroke-135"),sQuery(id+"F7.wireOp",EDGE,"E28.sketch_text.stroke-136"),sQuery(id+"F7.wireOp",EDGE,"E28.sketch_text.stroke-137"),sQuery(id+"F7.wireOp",EDGE,"E28.sketch_text.stroke-138"),sQuery(id+"F7.wireOp",EDGE,"E28.sketch_text.stroke-139")])],"isStart":false})});
            var Q8;
            Q8=makeQuery(id+"F8.boolean.opBoolean","COPY",FACE,{"derivedFrom":makeQuery(id+"F8.opExtrude","CAP_FACE",FACE,{"disambiguationData":[OSD([sQuery(id+"F7.wireOp",EDGE,"E28.sketch_text.stroke-140"),sQuery(id+"F7.wireOp",EDGE,"E28.sketch_text.stroke-141"),sQuery(id+"F7.wireOp",EDGE,"E28.sketch_text.stroke-142"),sQuery(id+"F7.wireOp",EDGE,"E28.sketch_text.stroke-143"),sQuery(id+"F7.wireOp",EDGE,"E28.sketch_text.stroke-144"),sQuery(id+"F7.wireOp",EDGE,"E28.sketch_text.stroke-145"),sQuery(id+"F7.wireOp",EDGE,"E28.sketch_text.stroke-146"),sQuery(id+"F7.wireOp",EDGE,"E28.sketch_text.stroke-147"),sQuery(id+"F7.wireOp",EDGE,"E28.sketch_text.stroke-148"),sQuery(id+"F7.wireOp",EDGE,"E28.sketch_text.stroke-149"),sQuery(id+"F7.wireOp",EDGE,"E28.sketch_text.stroke-150"),sQuery(id+"F7.wireOp",EDGE,"E28.sketch_text.stroke-151"),sQuery(id+"F7.wireOp",EDGE,"E28.sketch_text.stroke-152"),sQuery(id+"F7.wireOp",EDGE,"E28.sketch_text.stroke-153"),sQuery(id+"F7.wireOp",EDGE,"E28.sketch_text.stroke-154"),sQuery(id+"F7.wireOp",EDGE,"E28.sketch_text.stroke-155"),sQuery(id+"F7.wireOp",EDGE,"E28.sketch_text.stroke-156"),sQuery(id+"F7.wireOp",EDGE,"E28.sketch_text.stroke-157"),sQuery(id+"F7.wireOp",EDGE,"E28.sketch_text.stroke-158"),sQuery(id+"F7.wireOp",EDGE,"E28.sketch_text.stroke-159")])],"isStart":false})});
            var Q9;
            Q9=makeQuery(id+"F8.boolean.opBoolean","COPY",FACE,{"derivedFrom":makeQuery(id+"F8.opExtrude","CAP_FACE",FACE,{"disambiguationData":[OSD([sQuery(id+"F7.wireOp",EDGE,"E28.sketch_text.stroke-29"),sQuery(id+"F7.wireOp",EDGE,"E28.sketch_text.stroke-30"),sQuery(id+"F7.wireOp",EDGE,"E28.sketch_text.stroke-31"),sQuery(id+"F7.wireOp",EDGE,"E28.sketch_text.stroke-32"),sQuery(id+"F7.wireOp",EDGE,"E28.sketch_text.stroke-33"),sQuery(id+"F7.wireOp",EDGE,"E28.sketch_text.stroke-34"),sQuery(id+"F7.wireOp",EDGE,"E28.sketch_text.stroke-35"),sQuery(id+"F7.wireOp",EDGE,"E28.sketch_text.stroke-36")])],"isStart":false})});
            fillet(context, id + "F9", {"entities" : qUnion([Q0, Q1, Q2, Q3, Q4, Q5, Q6, Q7, Q8, Q9]), "radius" : 0.12 * mm, "tangentPropagation" : true, "allowEdgeOverflow" : false});
        }
    });
